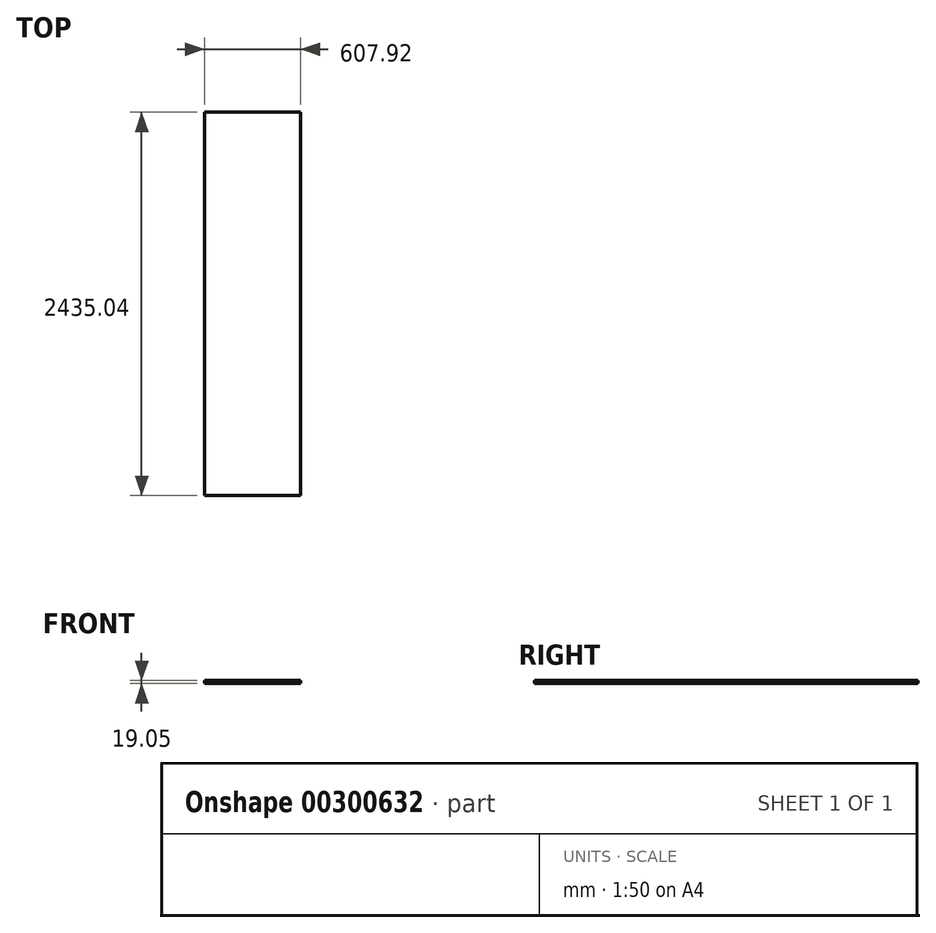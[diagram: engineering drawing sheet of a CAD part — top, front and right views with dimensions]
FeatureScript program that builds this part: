
annotation { "Feature Type Name" : "Feature", "Feature Type Description" : "" }
export const myFeature = defineFeature(function(context is Context, id is Id, definition is map)
    precondition{}
    {
        {
            var Q0;
            Q0=qCreatedBy(makeId("Top.planeOp"),FACE);
            var sketch = newSketch(context, id + "F0", { "sketchPlane" : qUnion([Q0])});
            skLineSegment(sketch, "E0.bottom", {"start": v(-303.96, -1217.52) * mm, "end": v(303.96, -1217.52) * mm});
            skLineSegment(sketch, "E0.top", {"start": v(-303.96, 1217.52) * mm, "end": v(303.96, 1217.52) * mm});
            skLineSegment(sketch, "E0.left", {"start": v(-303.96, -1217.52) * mm, "end": v(-303.96, 1217.52) * mm});
            skLineSegment(sketch, "E0.right", {"start": v(303.96, -1217.52) * mm, "end": v(303.96, 1217.52) * mm});
            skPoint(sketch, "E0.middle", {"position": v(0, 0) * mm});
            skSolve(sketch);
        }
        {
            var Q0;
            Q0=qSketchRegion(id+"F0",true);
            extrude(context, id + "F1", {"entities" : qUnion([Q0]), "depth" : 19.05 * mm});
        }
    });
